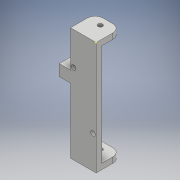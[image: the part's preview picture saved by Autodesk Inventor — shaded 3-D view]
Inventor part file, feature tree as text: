
AUTODESK INVENTOR PART (.ipt)
format: ipt  version: 2018 (Build 220112000, 112)  size: 201,728 bytes
history: native  units: mm
features: sketch x9, extrude x5, hole x3, fillet x2
ambient origin geometry x8: Origin, YZ Plane, XZ Plane, XY Plane, X Axis, Y Axis, Z Axis, Center Point
bodies: Solid1 (feature_tree)
feature tree (19):
  extrude  "Extrusion1"  Depth=100.0mm
  extrude  "Extrusion2"  Depth=5.0mm
  sketch  "Sketch3"  dims[d5=5.0mm d6=40.0mm d7=0.0mm]
  hole  "Hole1"  [1 undecoded]
  extrude  "Extrusion3"  Depth=2.0mm
  hole  "Hole2"  [1 undecoded]
  fillet  "Fillet1"  Radius=8.5mm
  extrude  "Extrusion4"  TaperAngle=90.0deg  [1 undecoded]
  extrude  "Extrusion5"  TaperAngle=180.0deg  [1 undecoded]
  hole  "Hole3"  [1 undecoded]
  fillet  "Fillet2"  Radius=3.5mm
  sketch  "Sketch1"  dims[d0=22.65mm d1=100.0mm]
  sketch  "Sketch2"  dims[d2=5.0mm d3=0.0mm d4=5.0mm]
  sketch  "Sketch4"  dims[d8=10.0mm]
  sketch  "Sketch5"  dims[d9=4.0mm d10=6.0mm d11=4.0mm d12=2.0mm d13=90.0deg d14=115.0mm d15=20.594885mm d16=23.0mm]
  sketch  "Sketch6"  dims[d17=102.75mm d18=0.0mm d19=1.175mm d20=8.5mm]
  sketch  "Sketch7"  dims[d21=21.0mm d22=90.0deg]
  sketch  "Sketch8"  dims[d23=8.5mm d24=180.0deg]
  sketch  "Sketch9"  dims[d25=21.0mm d26=4.0mm d27=6.0mm d28=4.0mm d29=2.0mm d30=90.0deg d31=115.0mm d32=20.594885mm d33=1.0mm d34=3.5mm d35=15.825mm d36=10.0mm d37=10.0mm d38=5.0mm d39=0.0mm d40=5.0mm d41=12.5mm d42=0.0mm d43=6.0mm d44=6.0mm d45=4.0mm d46=2.0mm d47=90.0deg d48=115.0mm d49=20.594885mm d50=7.0mm]
note: 5 required parameter values undecoded (feature->parameter linkage not recoverable at this tier; creation-order binding heuristic only, values carry confidence <= 0.55)
